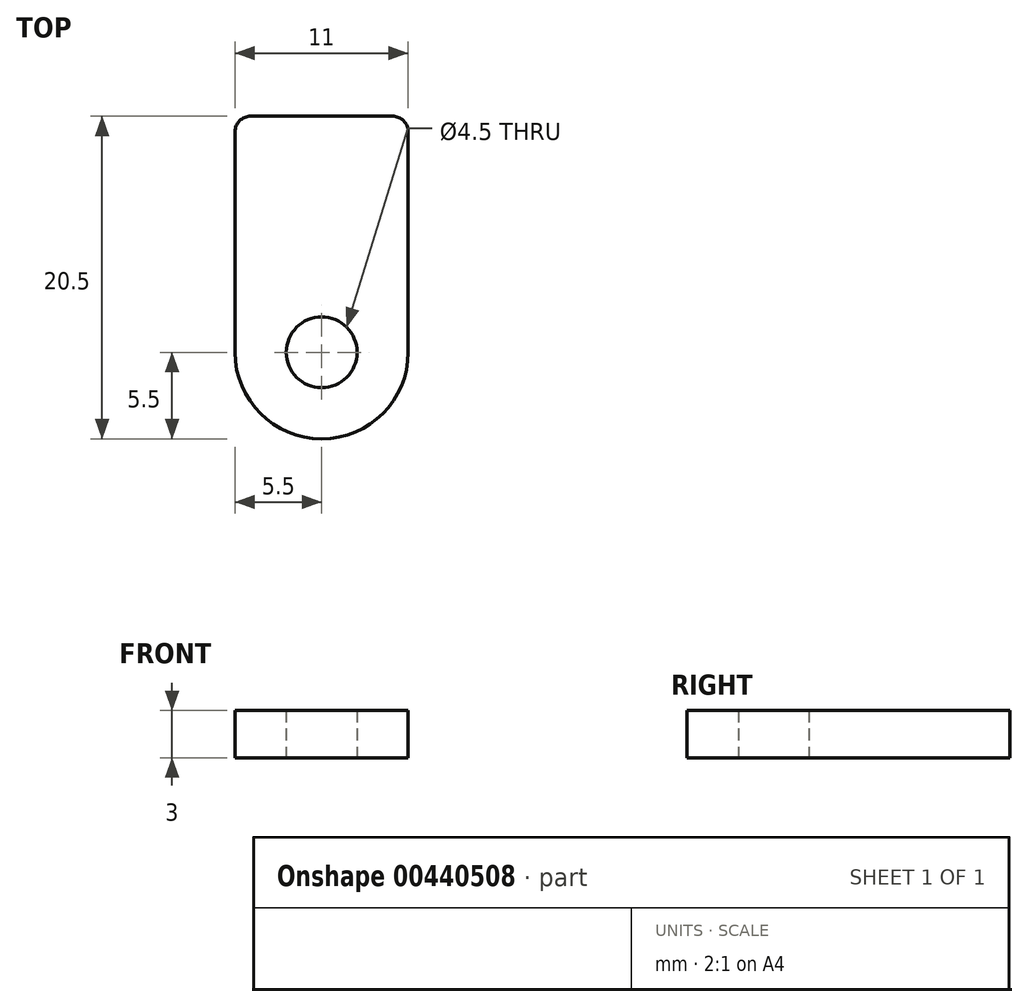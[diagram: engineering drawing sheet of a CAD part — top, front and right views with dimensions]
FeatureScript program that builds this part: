
annotation { "Feature Type Name" : "Feature", "Feature Type Description" : "" }
export const myFeature = defineFeature(function(context is Context, id is Id, definition is map)
    precondition{}
    {
        {
            var Q0;
            Q0=qCreatedBy(makeId("Top.planeOp"),FACE);
            var sketch = newSketch(context, id + "F0", { "sketchPlane" : qUnion([Q0])});
            skLineSegment(sketch, "E0", {"start": v(-5.5, 0) * mm, "end": v(-5.5, 14) * mm});
            skLineSegment(sketch, "E1", {"start": v(-4.5, 15) * mm, "end": v(4.5, 15) * mm});
            skLineSegment(sketch, "E2", {"start": v(5.5, 14) * mm, "end": v(5.5, 0) * mm});
            skArc(sketch, "E3", {"start": v(-5.5, 0) * mm, "mid": v(0, -5.5) * mm, "end": v(5.5, 0) * mm});
            skPoint(sketch, "E4.visualSharp", {"position": v(-5.5, 15) * mm});
            skArc(sketch, "E4.filletArc", {"start": v(-4.5, 15) * mm, "mid": v(-5.2, 14.7) * mm, "end": v(-5.5, 14) * mm});
            skPoint(sketch, "E5.visualSharp", {"position": v(5.5, 15) * mm});
            skArc(sketch, "E5.filletArc", {"start": v(5.5, 14) * mm, "mid": v(5.2, 14.7) * mm, "end": v(4.5, 15) * mm});
            skCircle(sketch, "E6", {"center": v(0, 0) * mm, "radius": 2.25 * mm});
            skSolve(sketch);
        }
        {
            var Q0;
            Q0=makeQuery(id+"F0.imprint","IMPRINT",FACE,{"disambiguationData":[TD([[makeQuery(id+"F0.imprint","IMPRINT",EDGE,{"derivedFrom":sQuery(id+"F0.wireOp",EDGE,"E0")}),-1.0]])]});
            extrude(context, id + "F1", {"entities" : qUnion([Q0]), "depth" : 3 * mm});
        }
    });
